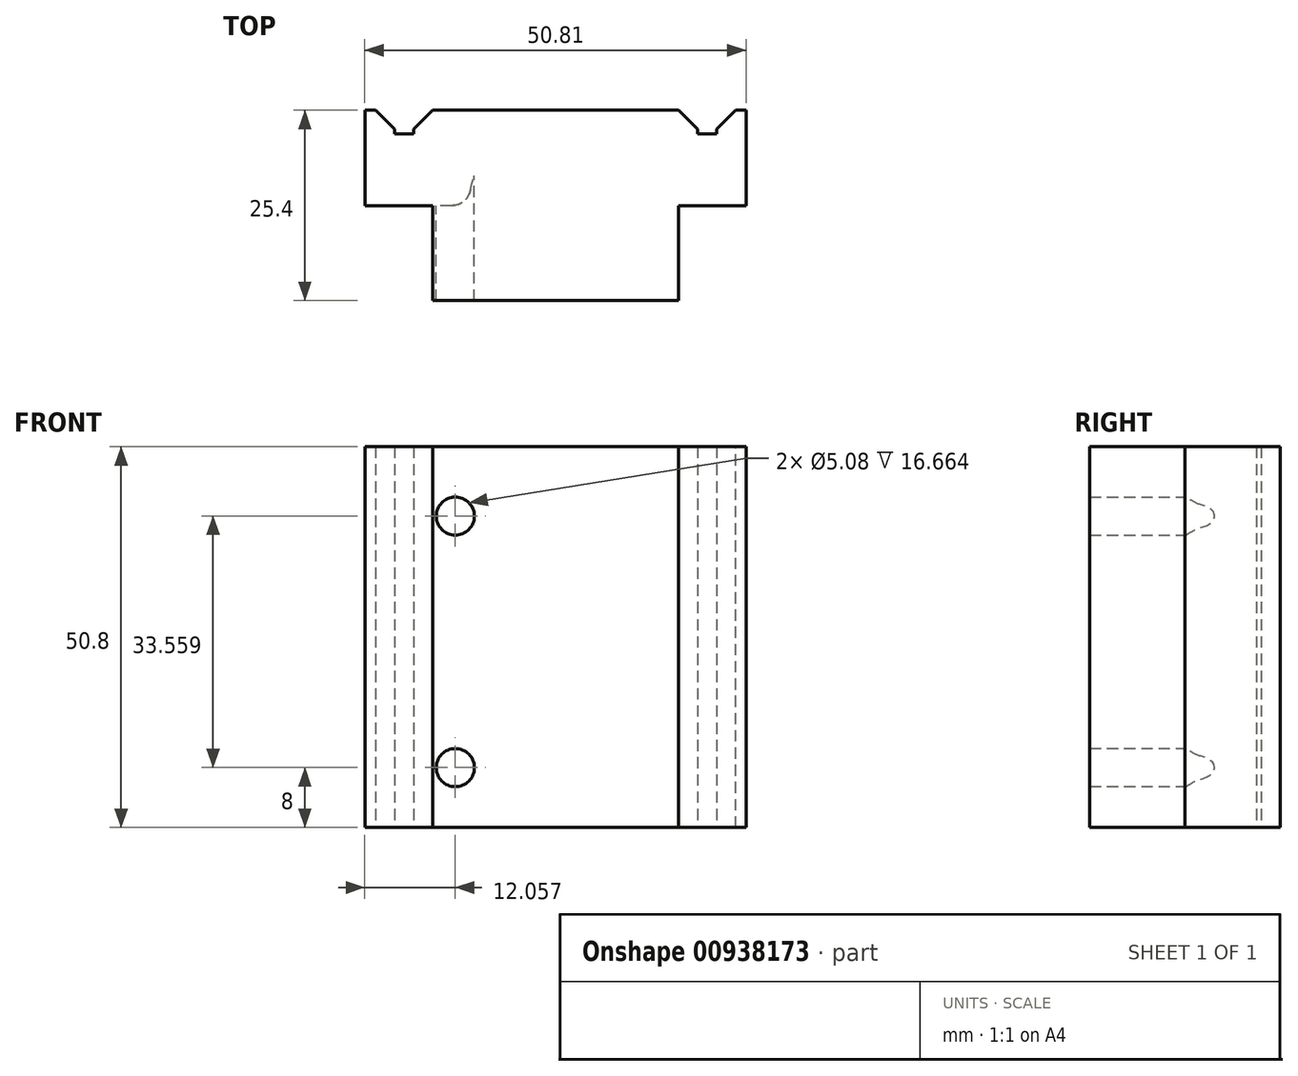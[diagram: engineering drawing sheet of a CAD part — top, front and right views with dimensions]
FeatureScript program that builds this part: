
annotation { "Feature Type Name" : "Feature", "Feature Type Description" : "" }
export const myFeature = defineFeature(function(context is Context, id is Id, definition is map)
    precondition{}
    {
        {
            var Q0;
            Q0=qCreatedBy(makeId("Top.planeOp"),FACE);
            var sketch = newSketch(context, id + "F0", { "sketchPlane" : qUnion([Q0])});
            skLineSegment(sketch, "E0", {"start": v(0, 0) * mm, "end": v(-25.4, 0) * mm});
            skLineSegment(sketch, "E1", {"start": v(-25.4, 0) * mm, "end": v(-25.4, 12.7) * mm});
            skLineSegment(sketch, "E2", {"start": v(-25.4, 12.7) * mm, "end": v(-21.45, 12.7) * mm});
            skLineSegment(sketch, "E3", {"start": v(-21.45, 12.7) * mm, "end": v(-21.45, 9.54) * mm});
            skLineSegment(sketch, "E4", {"start": v(-21.45, 9.54) * mm, "end": v(-18.9, 9.54) * mm});
            skLineSegment(sketch, "E5", {"start": v(-18.9, 9.54) * mm, "end": v(-18.9, 12.7) * mm});
            skLineSegment(sketch, "E6", {"start": v(-18.9, 12.7) * mm, "end": v(0, 12.7) * mm});
            skLineSegment(sketch, "E7", {"start": v(0, 12.7) * mm, "end": v(0, 0) * mm});
            skLineSegment(sketch, "E8", {"start": v(0, 0) * mm, "end": v(25.4, 0) * mm});
            skLineSegment(sketch, "E9", {"start": v(25.4, 0) * mm, "end": v(25.4, 12.7) * mm});
            skLineSegment(sketch, "E10", {"start": v(25.4, 12.7) * mm, "end": v(21.48, 12.7) * mm});
            skLineSegment(sketch, "E11", {"start": v(21.48, 12.7) * mm, "end": v(21.48, 9.54) * mm});
            skLineSegment(sketch, "E12", {"start": v(21.48, 9.54) * mm, "end": v(18.94, 9.54) * mm});
            skLineSegment(sketch, "E13", {"start": v(18.94, 9.54) * mm, "end": v(18.94, 12.7) * mm});
            skLineSegment(sketch, "E14", {"start": v(18.94, 12.7) * mm, "end": v(0, 12.7) * mm});
            skCircle(sketch, "E15", {"center": v(0, 0) * mm, "radius": 11.5 * mm});
            skSolve(sketch);
        }
        {
            var Q0;
            {var subQ0=sQuery(id+"F0.wireOp",EDGE,"E1");Q0=makeQuery(id+"F0.imprint","IMPRINT",FACE,{"disambiguationData":[TD([[makeQuery(id+"F0.imprint","IMPRINT",EDGE,{"derivedFrom":subQ0}),-1.0]])]});}
            var Q1;
            {var subQ0=sQuery(id+"F0.wireOp",EDGE,"E9");Q1=makeQuery(id+"F0.imprint","IMPRINT",FACE,{"disambiguationData":[TD([[makeQuery(id+"F0.imprint","IMPRINT",EDGE,{"derivedFrom":subQ0}),1.0]])]});}
            extrude(context, id + "F1", {"entities" : qUnion([Q0, Q1]), "depth" : 50.8 * mm, "offsetDistance" : 25.4 * mm});
        }
        {
            var Q0;
            Q0=makeQuery(id+"F1.opExtrude","SWEPT_EDGE",EDGE,{"disambiguationData":[OSD([sQuery(id+"F0.wireOp",EDGE,"E10"),sQuery(id+"F0.wireOp",EDGE,"E11")])]});
            chamfer(context, id + "F2", {"entities" : qUnion([Q0]), "width" : 2.54 * mm, "tangentPropagation" : true});
        }
        {
            var Q0;
            Q0=makeQuery(id+"F1.opExtrude","SWEPT_EDGE",EDGE,{"disambiguationData":[OSD([sQuery(id+"F0.wireOp",EDGE,"E2"),sQuery(id+"F0.wireOp",EDGE,"E3")])]});
            var Q1;
            Q1=makeQuery(id+"F1.opExtrude","SWEPT_EDGE",EDGE,{"disambiguationData":[OSD([sQuery(id+"F0.wireOp",EDGE,"E13"),sQuery(id+"F0.wireOp",EDGE,"E14")])]});
            chamfer(context, id + "F3", {"entities" : qUnion([Q0, Q1]), "width" : 2.54 * mm, "tangentPropagation" : true});
        }
        {
            var Q0;
            Q0=makeQuery(id+"F1.opExtrude","SWEPT_EDGE",EDGE,{"disambiguationData":[OSD([sQuery(id+"F0.wireOp",EDGE,"E5"),sQuery(id+"F0.wireOp",EDGE,"E6")])]});
            chamfer(context, id + "F4", {"entities" : qUnion([Q0]), "width" : 2.54 * mm, "tangentPropagation" : true});
        }
        {
            var Q0;
            Q0=makeQuery(id+"F1.opExtrude","SWEPT_EDGE",EDGE,{"disambiguationData":[OSD([sQuery(id+"F0.wireOp",EDGE,"E0"),sQuery(id+"F0.wireOp",EDGE,"E15")])]});
            var Q1;
            Q1=makeQuery(id+"F1.opExtrude","SWEPT_EDGE",EDGE,{"disambiguationData":[OSD([sQuery(id+"F0.wireOp",EDGE,"E8"),sQuery(id+"F0.wireOp",EDGE,"E15")])]});
            fillet(context, id + "F5", {"entities" : qUnion([Q0, Q1]), "radius" : 2.54 * mm, "tangentPropagation" : true, "allowEdgeOverflow" : false});
        }
        {
            var Q0;
            Q0=makeQuery(id+"F1.opExtrude","SWEPT_FACE",FACE,{"disambiguationData":[OSD([sQuery(id+"F0.wireOp",EDGE,"E6"),sQuery(id+"F0.wireOp",EDGE,"E14")])]});
            var sketch = newSketch(context, id + "F6", { "sketchPlane" : qUnion([Q0])});
            skCircle(sketch, "E16", {"center": v(-13.34, 41.56) * mm, "radius": 2.54 * mm});
            skCircle(sketch, "E17.MirrorC", {"center": v(13.34, 41.56) * mm, "radius": 2.54 * mm});
            skCircle(sketch, "E18", {"center": v(-13.34, 8) * mm, "radius": 2.54 * mm});
            skCircle(sketch, "E19.MirrorC", {"center": v(13.34, 8) * mm, "radius": 2.54 * mm});
            skSolve(sketch);
        }
        {
            var Q0;
            Q0=makeQuery(id+"F6.imprint","IMPRINT",FACE,{"disambiguationData":[TD([[makeQuery(id+"F6.imprint","IMPRINT",EDGE,{"derivedFrom":sQuery(id+"F6.wireOp",EDGE,"E16")}),1.0]])]});
            var Q1;
            Q1=makeQuery(id+"F6.imprint","IMPRINT",FACE,{"disambiguationData":[TD([[makeQuery(id+"F6.imprint","IMPRINT",EDGE,{"derivedFrom":sQuery(id+"F6.wireOp",EDGE,"E17.MirrorC")}),-1.0]])]});
            var Q2;
            Q2=makeQuery(id+"F6.imprint","IMPRINT",FACE,{"disambiguationData":[TD([[makeQuery(id+"F6.imprint","IMPRINT",EDGE,{"derivedFrom":sQuery(id+"F6.wireOp",EDGE,"E19.MirrorC")}),-1.0]])]});
            var Q3;
            Q3=makeQuery(id+"F6.imprint","IMPRINT",FACE,{"disambiguationData":[TD([[makeQuery(id+"F6.imprint","IMPRINT",EDGE,{"derivedFrom":sQuery(id+"F6.wireOp",EDGE,"E18")}),1.0]])]});
            extrude(context, id + "F7", {"entities" : qUnion([Q0, Q1, Q2, Q3]), "operationType" : NewBodyOperationType.ADD, "depth" : -25.4 * mm, "offsetDistance" : 25.4 * mm});
        }
    });
